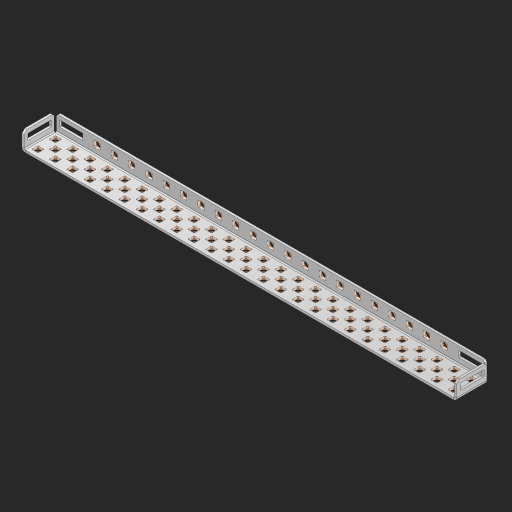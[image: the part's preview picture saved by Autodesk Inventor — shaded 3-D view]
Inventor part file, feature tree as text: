
AUTODESK INVENTOR PART (.ipt)
format: ipt  version: 2023 (Build 270158000, 158)  size: 1,636,352 bytes
history: native  units: in
note: dims shown in document units (in); Inventor stores cm internally (conversion verified against a paired STEP export)
features: other x96, extrude x95, pattern_linear x3, sketch x3, chamfer x1, move_body x1, imported_body x1
ambient origin geometry x8: Origin, YZ Plane, XZ Plane, XY Plane, X Axis, Y Axis, Z Axis, Center Point
bodies: Body1 (feature_tree), Body2 (feature_tree), Body3 (feature_tree), Body4 (feature_tree), Body5 (feature_tree), Body6 (feature_tree), Body7 (feature_tree), Body8 (feature_tree), Body9 (feature_tree), Body10 (feature_tree), Body11 (feature_tree), Body12 (feature_tree), Body13 (feature_tree), Body14 (feature_tree), Body15 (feature_tree), Body16 (feature_tree), Body17 (feature_tree), Body18 (feature_tree), Body19 (feature_tree), Body20 (feature_tree), Body21 (feature_tree), Body22 (feature_tree), Body23 (feature_tree), Body24 (feature_tree), Body25 (feature_tree), Body26 (feature_tree), Body27 (feature_tree), Body28 (feature_tree), Body29 (feature_tree), Body30 (feature_tree), Body31 (feature_tree), Body32 (feature_tree), Body33 (feature_tree), Body34 (feature_tree), Body35 (feature_tree), Body36 (feature_tree), Body37 (feature_tree), Body38 (feature_tree), Body39 (feature_tree), Body40 (feature_tree), Body41 (feature_tree), Body42 (feature_tree), Body43 (feature_tree), Body44 (feature_tree), Body45 (feature_tree), Body46 (feature_tree), Body47 (feature_tree), Body48 (feature_tree), Body49 (feature_tree), Body50 (feature_tree), Body51 (feature_tree), Body52 (feature_tree), Body53 (feature_tree), Body54 (feature_tree), Body55 (feature_tree), Body56 (feature_tree), Body57 (feature_tree), Body58 (feature_tree), Body59 (feature_tree), Body60 (feature_tree), Body61 (feature_tree), Body62 (feature_tree), Body63 (feature_tree), Body64 (feature_tree), Body65 (feature_tree), Body66 (feature_tree), Body67 (feature_tree), Body68 (feature_tree), Body69 (feature_tree), Body70 (feature_tree), Body71 (feature_tree), Body72 (feature_tree), Body73 (feature_tree), Body74 (feature_tree), Body75 (feature_tree), Body76 (feature_tree), Body77 (feature_tree), Body78 (feature_tree), Body79 (feature_tree), Body80 (feature_tree), Body81 (feature_tree), Body82 (feature_tree), Body83 (feature_tree), Body84 (feature_tree), Body85 (feature_tree), Body86 (feature_tree), Body87 (feature_tree), Body88 (feature_tree), Body89 (feature_tree), Body90 (feature_tree), Body91 (feature_tree), Body92 (feature_tree), Body93 (feature_tree), Body94 (feature_tree), Body95 (feature_tree), Body96 (feature_tree)
feature tree (200):
  chamfer  "Chamfer2"  Distance=0.063in
  other  "VL-RAIL-HH21-25 RevA1"
  move_body  "Move Body1"
  pattern_linear  "Rectangular Pattern1"  Count1=25 Spacing1=0.5in
  pattern_linear  "Rectangular Pattern2"  Spacing1=0.063in  [1 undecoded]
  pattern_linear  "Rectangular Pattern3"  Count1=24 Spacing1=0.5in
  imported_body  "Base1"
  sketch  "Sketch1"  dims[d0=180.0deg d1=-3.9725in d2=-0.1955in d3=2.3792in]
  other  "Srf1"
  other  "Srf2"
  other  "Srf3"
  other  "Srf4"
  other  "Srf5"
  other  "Srf6"
  other  "Srf7"
  other  "Srf8"
  other  "Srf9"
  other  "Srf10"
  other  "Srf11"
  other  "Srf12"
  other  "Srf13"
  other  "Srf14"
  other  "Srf15"
  other  "Srf16"
  other  "Srf17"
  other  "Srf18"
  other  "Srf19"
  other  "Srf20"
  other  "Srf21"
  other  "Srf22"
  other  "Srf23"
  other  "Srf24"
  other  "Srf25"
  other  "Srf26"
  other  "Srf27"
  other  "Srf28"
  other  "Srf29"
  other  "Srf30"
  other  "Srf31"
  other  "Srf32"
  other  "Srf33"
  other  "Srf34"
  other  "Srf35"
  other  "Srf36"
  other  "Srf37"
  other  "Srf38"
  other  "Srf39"
  other  "Srf40"
  other  "Srf41"
  other  "Srf42"
  other  "Srf43"
  other  "Srf44"
  other  "Srf45"
  other  "Srf46"
  other  "Srf47"
  other  "Srf48"
  other  "Srf49"
  other  "Srf50"
  sketch  "Sketch2"  dims[d4=0.182in d5=0.063in d6=0.0in d7=9.8425in d9=0.5in d10=0.7874in d12=0.5in]
  other  "Srf51"
  other  "Srf52"
  other  "Srf53"
  other  "Srf54"
  other  "Srf55"
  other  "Srf56"
  other  "Srf57"
  other  "Srf58"
  other  "Srf59"
  other  "Srf60"
  other  "Srf61"
  other  "Srf62"
  other  "Srf63"
  other  "Srf64"
  other  "Srf65"
  other  "Srf66"
  other  "Srf67"
  other  "Srf68"
  other  "Srf69"
  other  "Srf70"
  other  "Srf71"
  other  "Srf72"
  other  "Srf73"
  other  "Srf74"
  sketch  "Sketch3"  dims[d13=0.182in d14=0.063in d15=0.0in d16=9.4488in d18=0.5in d19=0.182in d20=0.063in d21=0.0in d22=8.2677in d24=0.5in d25=0.0in d26=0.0in d27=0.0in d28=0.0in d29=0.0in d30=0.0in d31=0.0in d32=0.0in d33=0.0in d34=0.0in d35=0.0in d36=0.0in d37=0.0in d38=0.0in d39=0.0in d40=0.0in d41=0.0in d42=0.0in d43=0.0in d44=0.0in d45=0.0in d46=0.0in d47=0.0in d48=0.0in d49=0.0in d50=0.0in d51=0.0in d52=0.0in d53=0.0in d54=0.0in d55=0.0in d56=0.0in d57=0.0in d58=0.0in d59=0.0in d60=0.0in d61=0.0in d62=0.0in d63=0.0in d64=0.0in d65=0.0in d66=0.0in d67=0.0in d68=0.0in d69=0.0in d70=0.0in d71=0.0in d72=0.0in d73=0.0in d74=0.0in d75=0.0in d76=0.0in d77=0.0in d78=0.0in d79=0.0in d80=0.0in d81=0.0in d82=0.0in d83=0.0in d84=0.0in d85=0.0in d86=0.0in d87=0.0in d88=0.0in d89=0.0in d90=0.0in d91=0.0in d92=0.0in d93=0.0in d94=0.0in d95=0.0in d96=0.0in d97=0.0in d98=0.0in d99=0.0in d100=0.0in d101=0.0in d102=0.0in d103=0.0in d104=0.0in d105=0.0in d106=0.0in d107=0.0in d108=0.0in d109=0.0in d110=0.0in d111=0.0in d112=0.0in d113=0.0in d114=0.0in d115=0.0in d116=0.0in d117=0.0in d118=0.0in d119=0.0in d120=0.0in d121=0.0in d122=0.0in d123=0.0in d124=0.0in d125=0.0in d126=0.0in d127=0.0in d128=0.0in d129=0.0in d130=0.0in d131=0.0in d132=0.0in d133=0.0in d134=0.0in d135=0.0in d136=0.0in d137=0.0in d138=0.0in d139=0.0in d140=0.0in d141=0.0in d142=0.0in d143=0.0in d144=0.0in d145=0.0in d146=0.0in d147=0.0in d148=0.0in d149=0.0in d150=0.0in d151=0.0in d152=0.0in d153=0.0in d154=0.0in d155=0.0in d156=0.0in d157=0.0in d158=0.0in d159=0.0in d160=0.0in d161=0.0in d162=0.0in d163=0.0in d164=0.0in d165=0.0in d166=0.0in d167=0.0in d168=0.0in d169=0.0in d170=0.0in d171=0.0in d172=0.0in d173=0.0in d174=0.0in d175=0.0in d176=0.0in d177=0.0in d178=0.0in d179=0.0in d180=0.0in d181=0.0in d182=0.0in d183=0.0in d184=0.0in d185=0.0in d186=0.0in d187=0.0in d188=0.0in d189=0.0in d190=0.0in d191=0.0in d192=0.0in d193=0.0in d194=0.0in d195=0.0in d196=0.0in d197=0.0in d198=0.0in d199=0.0in d200=0.0in d201=0.0in d202=0.0in d203=0.0in d204=0.0in d205=0.0in d206=0.0in d207=0.0in d208=0.0in d209=0.0in d210=0.0in d211=0.0in d212=0.0in d213=0.0in d214=0.0in]
  other  "Srf75"
  other  "Srf76"
  other  "Srf77"
  other  "Srf78"
  other  "Srf79"
  other  "Srf80"
  other  "Srf81"
  other  "Srf82"
  other  "Srf83"
  other  "Srf84"
  other  "Srf85"
  other  "Srf86"
  other  "Srf87"
  other  "Srf88"
  other  "Srf89"
  other  "Srf90"
  other  "Srf91"
  other  "Srf92"
  other  "Srf93"
  other  "Srf94"
  other  "Srf95"
  extrude  "ExtrusionSrf1"  Depth=0.182in
  extrude  "ExtrusionSrf51"  Depth=0.063in TaperAngle=0.0deg
  extrude  "ExtrusionSrf75"  Depth=0.5in
  extrude  "ExtrusionSrf2"  TaperAngle=0.0deg  [1 undecoded]
  extrude  "ExtrusionSrf3"  TaperAngle=0.0deg  [1 undecoded]
  extrude  "ExtrusionSrf4"  TaperAngle=0.0deg  [1 undecoded]
  extrude  "ExtrusionSrf5"  TaperAngle=0.0deg  [1 undecoded]
  extrude  "ExtrusionSrf6"  TaperAngle=0.0deg  [1 undecoded]
  extrude  "ExtrusionSrf7"  TaperAngle=0.0deg  [1 undecoded]
  extrude  "ExtrusionSrf8"  TaperAngle=0.0deg  [1 undecoded]
  extrude  "ExtrusionSrf9"  TaperAngle=0.0deg  [1 undecoded]
  extrude  "ExtrusionSrf10"  TaperAngle=0.0deg  [1 undecoded]
  extrude  "ExtrusionSrf11"  TaperAngle=0.0deg  [1 undecoded]
  extrude  "ExtrusionSrf12"  TaperAngle=0.0deg  [1 undecoded]
  extrude  "ExtrusionSrf13"  TaperAngle=0.0deg  [1 undecoded]
  extrude  "ExtrusionSrf14"  TaperAngle=0.0deg  [1 undecoded]
  extrude  "ExtrusionSrf15"  TaperAngle=0.0deg  [1 undecoded]
  extrude  "ExtrusionSrf16"  TaperAngle=0.0deg  [1 undecoded]
  extrude  "ExtrusionSrf17"  TaperAngle=0.0deg  [1 undecoded]
  extrude  "ExtrusionSrf18"  TaperAngle=0.0deg  [1 undecoded]
  extrude  "ExtrusionSrf19"  TaperAngle=0.0deg  [1 undecoded]
  extrude  "ExtrusionSrf20"  TaperAngle=0.0deg  [1 undecoded]
  extrude  "ExtrusionSrf21"  TaperAngle=0.0deg  [1 undecoded]
  extrude  "ExtrusionSrf22"  TaperAngle=0.0deg  [1 undecoded]
  extrude  "ExtrusionSrf23"  TaperAngle=0.0deg  [1 undecoded]
  extrude  "ExtrusionSrf24"  TaperAngle=0.0deg  [1 undecoded]
  extrude  "ExtrusionSrf25"  TaperAngle=0.0deg  [1 undecoded]
  extrude  "ExtrusionSrf26"  TaperAngle=0.0deg  [1 undecoded]
  extrude  "ExtrusionSrf27"  TaperAngle=0.0deg  [1 undecoded]
  extrude  "ExtrusionSrf28"  TaperAngle=0.0deg  [1 undecoded]
  extrude  "ExtrusionSrf29"  TaperAngle=0.0deg  [1 undecoded]
  extrude  "ExtrusionSrf30"  TaperAngle=0.0deg  [1 undecoded]
  extrude  "ExtrusionSrf31"  TaperAngle=0.0deg  [1 undecoded]
  extrude  "ExtrusionSrf32"  TaperAngle=0.0deg  [1 undecoded]
  extrude  "ExtrusionSrf33"  TaperAngle=0.0deg  [1 undecoded]
  extrude  "ExtrusionSrf34"  TaperAngle=0.0deg  [1 undecoded]
  extrude  "ExtrusionSrf35"  TaperAngle=0.0deg  [1 undecoded]
  extrude  "ExtrusionSrf36"  TaperAngle=0.0deg  [1 undecoded]
  extrude  "ExtrusionSrf37"  TaperAngle=0.0deg  [1 undecoded]
  extrude  "ExtrusionSrf38"  TaperAngle=0.0deg  [1 undecoded]
  extrude  "ExtrusionSrf39"  TaperAngle=0.0deg  [1 undecoded]
  extrude  "ExtrusionSrf40"  TaperAngle=0.0deg  [1 undecoded]
  extrude  "ExtrusionSrf41"  TaperAngle=0.0deg  [1 undecoded]
  extrude  "ExtrusionSrf42"  TaperAngle=0.0deg  [1 undecoded]
  extrude  "ExtrusionSrf43"  TaperAngle=0.0deg  [1 undecoded]
  extrude  "ExtrusionSrf44"  TaperAngle=0.0deg  [1 undecoded]
  extrude  "ExtrusionSrf45"  TaperAngle=0.0deg  [1 undecoded]
  extrude  "ExtrusionSrf46"  TaperAngle=0.0deg  [1 undecoded]
  extrude  "ExtrusionSrf47"  TaperAngle=0.0deg  [1 undecoded]
  extrude  "ExtrusionSrf48"  TaperAngle=0.0deg  [1 undecoded]
  extrude  "ExtrusionSrf49"  TaperAngle=0.0deg  [1 undecoded]
  extrude  "ExtrusionSrf50"  TaperAngle=0.0deg  [1 undecoded]
  extrude  "ExtrusionSrf52"  TaperAngle=0.0deg  [1 undecoded]
  extrude  "ExtrusionSrf53"  TaperAngle=0.0deg  [1 undecoded]
  extrude  "ExtrusionSrf54"  TaperAngle=0.0deg  [1 undecoded]
  extrude  "ExtrusionSrf55"  TaperAngle=0.0deg  [1 undecoded]
  extrude  "ExtrusionSrf56"  TaperAngle=0.0deg  [1 undecoded]
  extrude  "ExtrusionSrf57"  TaperAngle=0.0deg  [1 undecoded]
  extrude  "ExtrusionSrf58"  TaperAngle=0.0deg  [1 undecoded]
  extrude  "ExtrusionSrf59"  TaperAngle=0.0deg  [1 undecoded]
  extrude  "ExtrusionSrf60"  TaperAngle=0.0deg  [1 undecoded]
  extrude  "ExtrusionSrf61"  TaperAngle=0.0deg  [1 undecoded]
  extrude  "ExtrusionSrf62"  TaperAngle=0.0deg  [1 undecoded]
  extrude  "ExtrusionSrf63"  TaperAngle=0.0deg  [1 undecoded]
  extrude  "ExtrusionSrf64"  TaperAngle=0.0deg  [1 undecoded]
  extrude  "ExtrusionSrf65"  TaperAngle=0.0deg  [1 undecoded]
  extrude  "ExtrusionSrf66"  TaperAngle=0.0deg  [1 undecoded]
  extrude  "ExtrusionSrf67"  TaperAngle=0.0deg  [1 undecoded]
  extrude  "ExtrusionSrf68"  TaperAngle=0.0deg  [1 undecoded]
  extrude  "ExtrusionSrf69"  TaperAngle=0.0deg  [1 undecoded]
  extrude  "ExtrusionSrf70"  TaperAngle=0.0deg  [1 undecoded]
  extrude  "ExtrusionSrf71"  TaperAngle=0.0deg  [1 undecoded]
  extrude  "ExtrusionSrf72"  TaperAngle=0.0deg  [1 undecoded]
  extrude  "ExtrusionSrf73"  TaperAngle=0.0deg  [1 undecoded]
  extrude  "ExtrusionSrf74"  TaperAngle=0.0deg  [1 undecoded]
  extrude  "ExtrusionSrf76"  TaperAngle=0.0deg  [1 undecoded]
  extrude  "ExtrusionSrf77"  TaperAngle=0.0deg  [1 undecoded]
  extrude  "ExtrusionSrf78"  TaperAngle=0.0deg  [1 undecoded]
  extrude  "ExtrusionSrf79"  TaperAngle=0.0deg  [1 undecoded]
  extrude  "ExtrusionSrf80"  TaperAngle=0.0deg  [1 undecoded]
  extrude  "ExtrusionSrf81"  TaperAngle=0.0deg  [1 undecoded]
  extrude  "ExtrusionSrf82"  TaperAngle=0.0deg  [1 undecoded]
  extrude  "ExtrusionSrf83"  TaperAngle=0.0deg  [1 undecoded]
  extrude  "ExtrusionSrf84"  TaperAngle=0.0deg  [1 undecoded]
  extrude  "ExtrusionSrf85"  TaperAngle=0.0deg  [1 undecoded]
  extrude  "ExtrusionSrf86"  TaperAngle=0.0deg  [1 undecoded]
  extrude  "ExtrusionSrf87"  TaperAngle=0.0deg  [1 undecoded]
  extrude  "ExtrusionSrf88"  TaperAngle=0.0deg  [1 undecoded]
  extrude  "ExtrusionSrf89"  TaperAngle=0.0deg  [1 undecoded]
  extrude  "ExtrusionSrf90"  TaperAngle=0.0deg  [1 undecoded]
  extrude  "ExtrusionSrf91"  TaperAngle=0.0deg  [1 undecoded]
  extrude  "ExtrusionSrf92"  TaperAngle=0.0deg  [1 undecoded]
  extrude  "ExtrusionSrf93"  TaperAngle=0.0deg  [1 undecoded]
  extrude  "ExtrusionSrf94"  TaperAngle=0.0deg  [1 undecoded]
  extrude  "ExtrusionSrf95"  TaperAngle=0.0deg  [1 undecoded]
note: 93 required parameter values undecoded (feature->parameter linkage not recoverable at this tier; creation-order binding heuristic only, values carry confidence <= 0.55)
